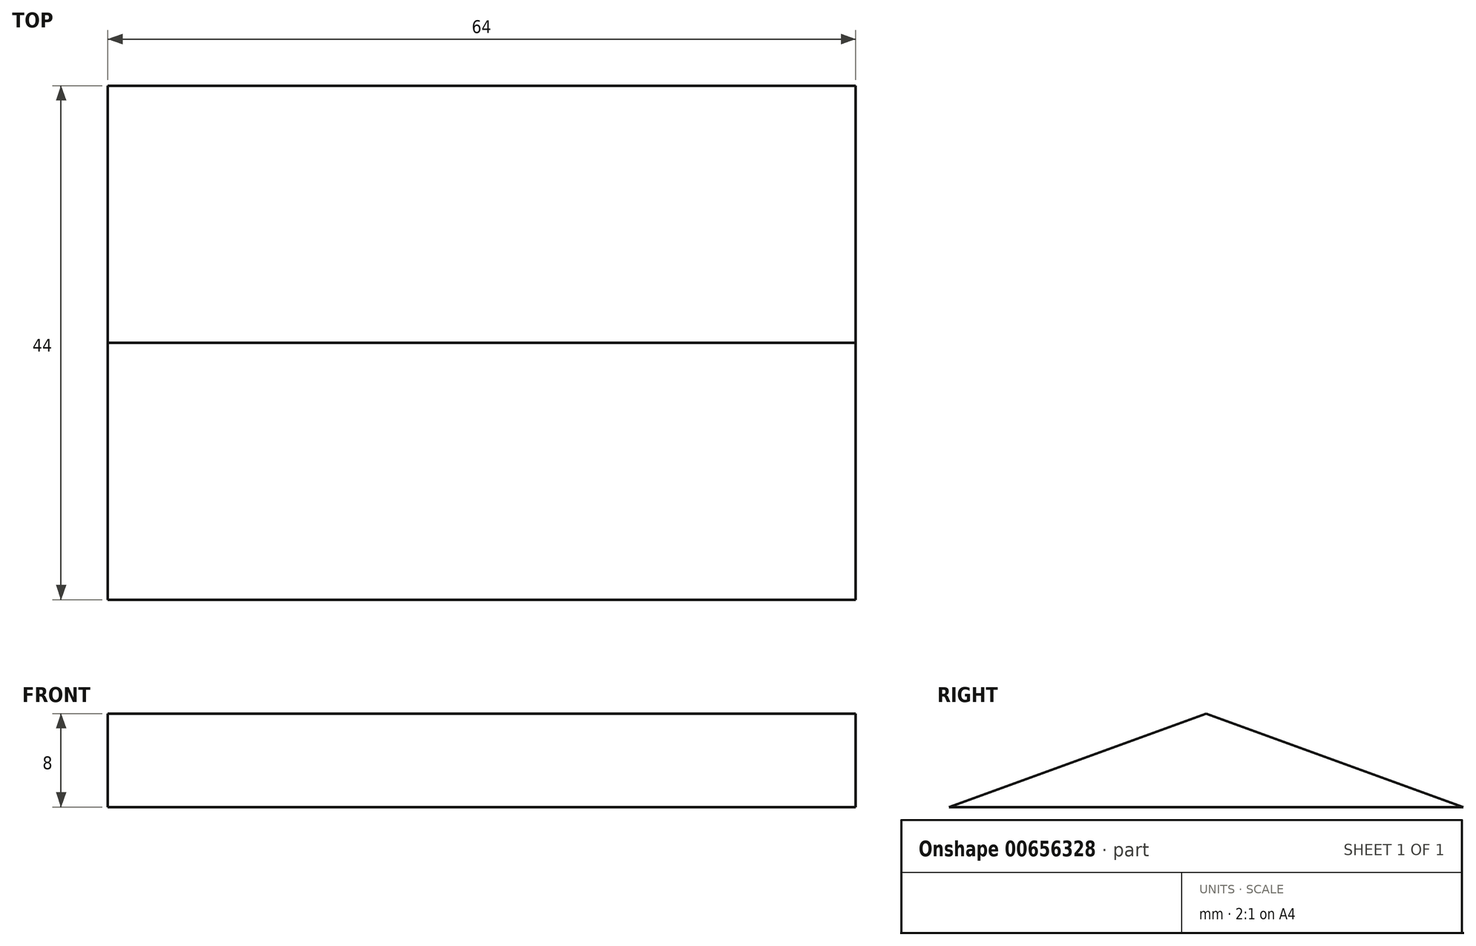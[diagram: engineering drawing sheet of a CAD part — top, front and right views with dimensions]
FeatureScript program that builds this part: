
annotation { "Feature Type Name" : "Feature", "Feature Type Description" : "" }
export const myFeature = defineFeature(function(context is Context, id is Id, definition is map)
    precondition{}
    {
        {
            var Q0;
            Q0=qCreatedBy(makeId("Top.planeOp"),FACE);
            var sketch = newSketch(context, id + "F0", { "sketchPlane" : qUnion([Q0])});
            skLineSegment(sketch, "E0.bottom", {"start": v(32, 22) * mm, "end": v(-32, 22) * mm});
            skLineSegment(sketch, "E0.top", {"start": v(32, -22) * mm, "end": v(-32, -22) * mm});
            skLineSegment(sketch, "E0.left", {"start": v(32, 22) * mm, "end": v(32, -22) * mm});
            skLineSegment(sketch, "E0.right", {"start": v(-32, 22) * mm, "end": v(-32, -22) * mm});
            skPoint(sketch, "E0.middle", {"position": v(0, 0) * mm});
            skSolve(sketch);
        }
        {
            var Q0;
            Q0=makeQuery(id+"F0.imprint","IMPRINT",FACE,{"disambiguationData":[TD([[makeQuery(id+"F0.imprint","IMPRINT",EDGE,{"derivedFrom":sQuery(id+"F0.wireOp",EDGE,"E0.bottom")}),1.0]])]});
            extrude(context, id + "F1", {"entities" : qUnion([Q0]), "depth" : 8 * mm, "offsetDistance" : 25 * mm});
        }
        {
            var Q0;
            Q0=makeQuery(id+"F1.opExtrude","CAP_EDGE",EDGE,{"disambiguationData":[OSD([sQuery(id+"F0.wireOp",EDGE,"E0.top")])],"isStart":false});
            var Q1;
            Q1=makeQuery(id+"F1.opExtrude","CAP_EDGE",EDGE,{"disambiguationData":[OSD([sQuery(id+"F0.wireOp",EDGE,"E0.bottom")])],"isStart":false});
            chamfer(context, id + "F2", {"entities" : qUnion([Q0, Q1]), "chamferType" : ChamferType.TWO_OFFSETS, "width1" : 8 * mm, "oppositeDirection" : false, "width2" : 22 * mm, "tangentPropagation" : true});
        }
    });
